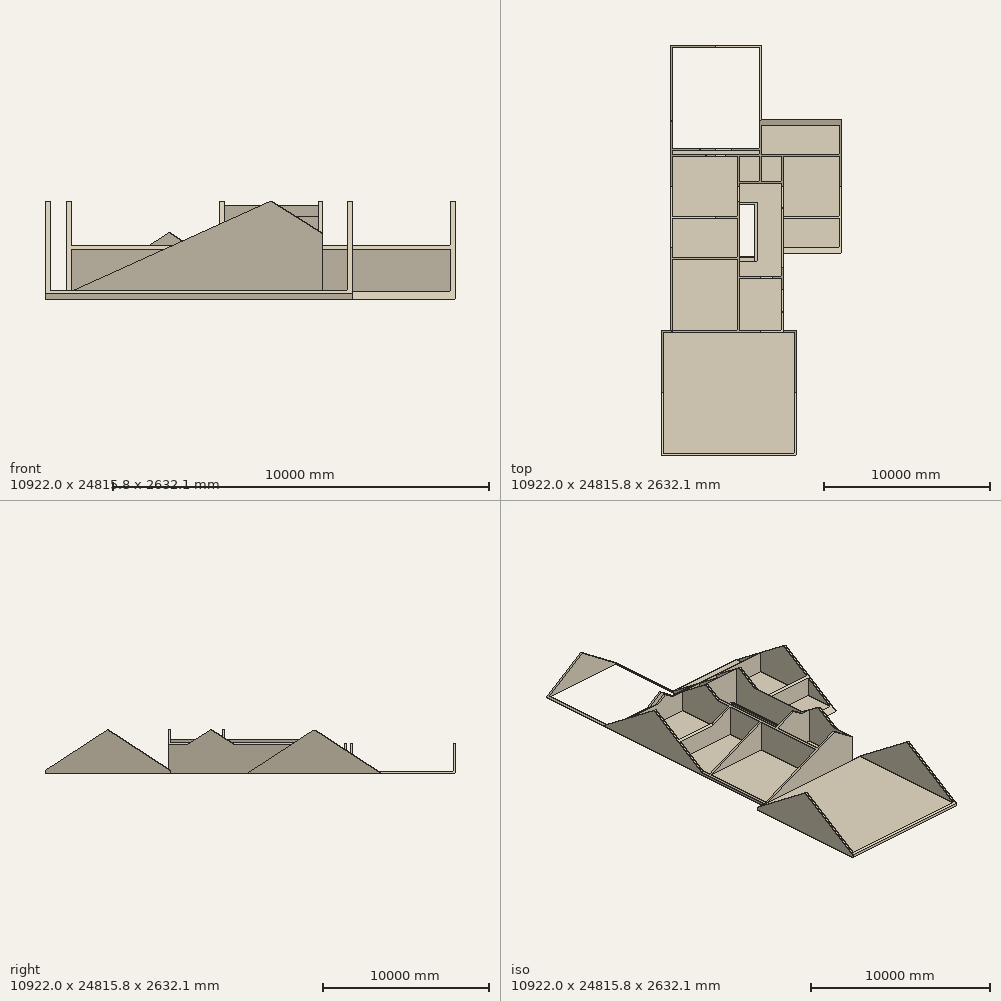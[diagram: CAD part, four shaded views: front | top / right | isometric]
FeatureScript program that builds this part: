
annotation { "Feature Type Name" : "Feature", "Feature Type Description" : "" }
export const myFeature = defineFeature(function(context is Context, id is Id, definition is map)
    precondition{}
    {
        {
            var Q0;
            Q0=qCreatedBy(makeId("Top.planeOp"),FACE);
            var sketch = newSketch(context, id + "F0", { "sketchPlane" : qUnion([Q0])});
            skLineSegment(sketch, "E0", {"start": v(0, 0) * mm, "end": v(8178.8, 0) * mm});
            skLineSegment(sketch, "E1", {"start": v(0, 0) * mm, "end": v(0, 7569.2) * mm});
            skLineSegment(sketch, "E2", {"start": v(0, 7569.2) * mm, "end": v(558.8, 7569.2) * mm});
            skLineSegment(sketch, "E3", {"start": v(558.8, 7569.2) * mm, "end": v(558.8, 24815.8) * mm});
            skLineSegment(sketch, "E4", {"start": v(558.8, 24815.8) * mm, "end": v(6045.2, 24815.8) * mm});
            skLineSegment(sketch, "E5", {"start": v(6045.2, 24815.8) * mm, "end": v(6045.2, 20548.6) * mm});
            skLineSegment(sketch, "E6", {"start": v(6045.2, 20548.6) * mm, "end": v(10922, 20548.6) * mm});
            skLineSegment(sketch, "E7", {"start": v(10922, 20548.6) * mm, "end": v(10922, 12014.2) * mm});
            skLineSegment(sketch, "E8", {"start": v(10922, 12014.2) * mm, "end": v(7391.4, 12014.2) * mm});
            skLineSegment(sketch, "E9", {"start": v(7391.4, 12014.2) * mm, "end": v(7391.4, 7569.2) * mm});
            skLineSegment(sketch, "E10", {"start": v(7391.4, 7569.2) * mm, "end": v(8178.8, 7569.2) * mm});
            skLineSegment(sketch, "E11", {"start": v(8178.8, 7569.2) * mm, "end": v(8178.8, 0) * mm});
            skSolve(sketch);
        }
        {
            var Q0;
            Q0=qSketchRegion(id+"F0",true);
            extrude(context, id + "F1", {"entities" : qUnion([Q0]), "depth" : 2632.07 * mm});
        }
        {
            var Q0;
            Q0=makeQuery(id+"F1.opExtrude","SWEPT_FACE",FACE,{"disambiguationData":[OSD([sQuery(id+"F0.wireOp",EDGE,"E7")])]});
            var sketch = newSketch(context, id + "F2", { "sketchPlane" : qUnion([Q0])});
            skLineSegment(sketch, "E12", {"start": v(16281.4, 2632.08) * mm, "end": v(16281.4, 219.08) * mm, "construction": true});
            skLineSegment(sketch, "E13", {"start": v(14452.6, 219.08) * mm, "end": v(18110.2, 219.08) * mm, "construction": true});
            skLineSegment(sketch, "E14", {"start": v(14452.6, 219.08) * mm, "end": v(14452.6, 1438.28) * mm, "construction": true});
            skLineSegment(sketch, "E15", {"start": v(16281.4, 2632.08) * mm, "end": v(12249.29, 0) * mm});
            skLineSegment(sketch, "E16", {"start": v(12249.29, 0) * mm, "end": v(12014.2, 0) * mm});
            skLineSegment(sketch, "E17", {"start": v(12014.2, 0) * mm, "end": v(12014.2, 2632.08) * mm});
            skLineSegment(sketch, "E18", {"start": v(12014.2, 2632.08) * mm, "end": v(16281.4, 2632.08) * mm});
            skLineSegment(sketch, "E19.MirrorCS", {"start": v(16281.4, 2632.08) * mm, "end": v(20313.51, 0) * mm});
            skLineSegment(sketch, "E20.MirrorCS", {"start": v(20313.51, 0) * mm, "end": v(20548.6, 0) * mm});
            skLineSegment(sketch, "E21.MirrorCS", {"start": v(20548.6, 0) * mm, "end": v(20548.6, 2632.08) * mm});
            skLineSegment(sketch, "E22.MirrorCS", {"start": v(20548.6, 2632.08) * mm, "end": v(16281.4, 2632.08) * mm});
            skLineSegment(sketch, "E23", {"start": v(3784.6, 2632.08) * mm, "end": v(3784.6, 219.08) * mm, "construction": true});
            skLineSegment(sketch, "E24", {"start": v(1955.8, 219.08) * mm, "end": v(5613.4, 219.08) * mm, "construction": true});
            skLineSegment(sketch, "E25", {"start": v(1955.8, 219.08) * mm, "end": v(1955.8, 1438.28) * mm, "construction": true});
            skLineSegment(sketch, "E26", {"start": v(3784.6, 2632.08) * mm, "end": v(0, 161.57) * mm});
            skLineSegment(sketch, "E27", {"start": v(0, 161.57) * mm, "end": v(0, 2632.08) * mm});
            skLineSegment(sketch, "E28", {"start": v(0, 2632.08) * mm, "end": v(3784.6, 2632.08) * mm});
            skLineSegment(sketch, "E29.MirrorCS", {"start": v(3784.6, 2632.08) * mm, "end": v(7569.2, 161.57) * mm});
            skLineSegment(sketch, "E30.MirrorCS", {"start": v(7569.2, 161.57) * mm, "end": v(7569.2, 2632.08) * mm});
            skLineSegment(sketch, "E31.MirrorCS", {"start": v(7569.2, 2632.08) * mm, "end": v(3784.6, 2632.08) * mm});
            skSolve(sketch);
        }
        {
            var Q0;
            Q0=qSketchRegion(id+"F2",true);
            var Q1;
            Q1=makeQuery(id+"F1.opExtrude","SWEPT_FACE",FACE,{"disambiguationData":[OSD([sQuery(id+"F0.wireOp",EDGE,"E1")])]});
            extrude(context, id + "F3", {"entities" : qUnion([Q0]), "operationType" : NewBodyOperationType.REMOVE, "endBound" : BoundingType.UP_TO_SURFACE, "oppositeDirection" : true, "endBoundEntityFace" : qUnion([Q1]), "depth" : 25.4 * mm});
        }
        {
            var Q0;
            Q0=makeQuery(id+"F3.boolean.opBoolean","COPY",FACE,{"derivedFrom":makeQuery(id+"F3.opExtrude","SWEPT_FACE",FACE,{"disambiguationData":[OSD([sQuery(id+"F2.wireOp",EDGE,"E30.MirrorCS")])]})});
            var sketch = newSketch(context, id + "F4", { "sketchPlane" : qUnion([Q0])});
            skLineSegment(sketch, "E32", {"start": v(6010.28, 2632.07) * mm, "end": v(6010.28, 219.07) * mm, "construction": true});
            skLineSegment(sketch, "E33", {"start": v(4756.15, 219.07) * mm, "end": v(7264.4, 219.07) * mm, "construction": true});
            skLineSegment(sketch, "E34", {"start": v(4756.15, 219.07) * mm, "end": v(4756.15, 1844.67) * mm, "construction": true});
            skLineSegment(sketch, "E35", {"start": v(6010.28, 2632.08) * mm, "end": v(558.8, 161.57) * mm});
            skLineSegment(sketch, "E36", {"start": v(558.8, 161.57) * mm, "end": v(558.8, 2632.07) * mm});
            skLineSegment(sketch, "E37", {"start": v(558.8, 2632.07) * mm, "end": v(6010.28, 2632.07) * mm});
            skLineSegment(sketch, "E38.MirrorCS", {"start": v(7264.4, 219.07) * mm, "end": v(7264.4, 1844.67) * mm, "construction": true});
            skLineSegment(sketch, "E39", {"start": v(6010.27, 2632.08) * mm, "end": v(7391.4, 1764.94) * mm});
            skLineSegment(sketch, "E40", {"start": v(7391.4, 1764.94) * mm, "end": v(7391.4, 2632.07) * mm});
            skLineSegment(sketch, "E41", {"start": v(7391.4, 2632.07) * mm, "end": v(6010.28, 2632.07) * mm});
            skSolve(sketch);
        }
        {
            var Q0;
            Q0=qSketchRegion(id+"F4",true);
            extrude(context, id + "F5", {"entities" : qUnion([Q0]), "operationType" : NewBodyOperationType.REMOVE, "endBound" : BoundingType.UP_TO_NEXT, "oppositeDirection" : true, "depth" : 25.4 * mm});
        }
        {
            var Q0;
            Q0=makeQuery(id+"F3.boolean.opBoolean","COPY",FACE,{"derivedFrom":makeQuery(id+"F3.opExtrude","SWEPT_FACE",FACE,{"disambiguationData":[OSD([sQuery(id+"F2.wireOp",EDGE,"E30.MirrorCS")])]})});
            var sketch = newSketch(context, id + "F6", { "sketchPlane" : qUnion([Q0])});
            skLineSegment(sketch, "E42", {"start": v(558.8, 161.57) * mm, "end": v(6010.28, 2632.08) * mm});
            skLineSegment(sketch, "E43", {"start": v(6010.28, 2632.08) * mm, "end": v(7391.4, 1764.94) * mm});
            skLineSegment(sketch, "E44", {"start": v(7391.4, 1764.94) * mm, "end": v(7391.4, 161.57) * mm});
            skLineSegment(sketch, "E45", {"start": v(7391.4, 161.57) * mm, "end": v(558.8, 161.57) * mm});
            skSolve(sketch);
        }
        {
            var Q0;
            Q0=qSketchRegion(id+"F6",true);
            extrude(context, id + "F7", {"entities" : qUnion([Q0]), "operationType" : NewBodyOperationType.ADD, "endBound" : BoundingType.UP_TO_NEXT, "depth" : 25.4 * mm});
        }
        {
            var Q0;
            Q0=makeQuery(id+"F3.boolean.opBoolean","COPY",FACE,{"derivedFrom":makeQuery(id+"F3.opExtrude","SWEPT_FACE",FACE,{"disambiguationData":[OSD([sQuery(id+"F2.wireOp",EDGE,"E17")])]})});
            var sketch = newSketch(context, id + "F8", { "sketchPlane" : qUnion([Q0])});
            skLineSegment(sketch, "E46", {"start": v(-6010.27, 2632.08) * mm, "end": v(-7391.4, 1764.94) * mm});
            skLineSegment(sketch, "E47", {"start": v(-7391.4, 1764.94) * mm, "end": v(-7391.4, 0) * mm});
            skLineSegment(sketch, "E48", {"start": v(-7391.4, 0) * mm, "end": v(-558.8, 0) * mm});
            skLineSegment(sketch, "E49", {"start": v(-558.8, 161.57) * mm, "end": v(-6010.27, 2632.08) * mm});
            skLineSegment(sketch, "E50", {"start": v(-558.8, 161.57) * mm, "end": v(-558.8, 0) * mm});
            skSolve(sketch);
        }
        {
            var Q0;
            Q0=qSketchRegion(id+"F8",true);
            extrude(context, id + "F9", {"entities" : qUnion([Q0]), "operationType" : NewBodyOperationType.ADD, "endBound" : BoundingType.UP_TO_NEXT, "depth" : 25.4 * mm});
        }
        {
            var Q0;
            Q0=makeQuery(id+"F1.opExtrude","SWEPT_FACE",FACE,{"disambiguationData":[OSD([sQuery(id+"F0.wireOp",EDGE,"E4")])]});
            var sketch = newSketch(context, id + "F10", { "sketchPlane" : qUnion([Q0])});
            skLineSegment(sketch, "E51", {"start": v(-3302, 2632.08) * mm, "end": v(-3302, 0) * mm, "construction": true});
            skPoint(sketch, "E52", {"position": v(-3302, 219.07) * mm});
            skPoint(sketch, "E53", {"position": v(-3302, 1793.88) * mm});
            skLineSegment(sketch, "E54", {"start": v(-5130.8, 219.07) * mm, "end": v(-1473.2, 219.07) * mm, "construction": true});
            skLineSegment(sketch, "E55", {"start": v(-5130.8, 219.08) * mm, "end": v(-5130.8, 1438.27) * mm, "construction": true});
            skLineSegment(sketch, "E56", {"start": v(-5130.8, 1438.27) * mm, "end": v(-3302, 2632.08) * mm, "construction": true});
            skLineSegment(sketch, "E57", {"start": v(-3302, 1793.88) * mm, "end": v(-6045.2, 3.17) * mm});
            skLineSegment(sketch, "E58", {"start": v(-6045.2, 3.17) * mm, "end": v(-6045.2, 2632.08) * mm});
            skLineSegment(sketch, "E59", {"start": v(-6045.2, 2632.08) * mm, "end": v(-3302, 2632.08) * mm});
            skLineSegment(sketch, "E60.MirrorCS", {"start": v(-3302, 1793.88) * mm, "end": v(-558.8, 3.17) * mm});
            skLineSegment(sketch, "E61.MirrorCS", {"start": v(-558.8, 3.17) * mm, "end": v(-558.8, 2632.08) * mm});
            skLineSegment(sketch, "E62.MirrorCS", {"start": v(-558.8, 2632.08) * mm, "end": v(-3302, 2632.08) * mm});
            skSolve(sketch);
        }
        {
            var Q0;
            Q0=qSketchRegion(id+"F10",true);
            extrude(context, id + "F11", {"entities" : qUnion([Q0]), "operationType" : NewBodyOperationType.REMOVE, "endBound" : BoundingType.UP_TO_NEXT, "oppositeDirection" : true, "depth" : 25.4 * mm});
        }
        {
            var Q0;
            Q0=makeQuery(id+"F3.boolean.opBoolean","COPY",FACE,{"derivedFrom":makeQuery(id+"F3.opExtrude","SWEPT_FACE",FACE,{"disambiguationData":[OSD([sQuery(id+"F2.wireOp",EDGE,"E21.MirrorCS")])]})});
            var sketch = newSketch(context, id + "F12", { "sketchPlane" : qUnion([Q0])});
            skLineSegment(sketch, "E63", {"start": v(3302, 1793.88) * mm, "end": v(558.8, 3.17) * mm});
            skLineSegment(sketch, "E64", {"start": v(558.8, 3.17) * mm, "end": v(558.8, 0) * mm});
            skLineSegment(sketch, "E65", {"start": v(558.8, 0) * mm, "end": v(6045.2, 0) * mm});
            skLineSegment(sketch, "E66", {"start": v(6045.2, 0) * mm, "end": v(6045.2, 3.17) * mm});
            skLineSegment(sketch, "E67", {"start": v(6045.2, 3.17) * mm, "end": v(3302, 1793.88) * mm});
            skSolve(sketch);
        }
        {
            var Q0;
            Q0=qSketchRegion(id+"F12",true);
            extrude(context, id + "F13", {"entities" : qUnion([Q0]), "operationType" : NewBodyOperationType.ADD, "endBound" : BoundingType.UP_TO_NEXT, "depth" : 25.4 * mm});
        }
        {
            var Q0;
            Q0=makeQuery(id+"F9.boolean.opBoolean","MERGE",FACE,{"derivedFrom":[makeQuery(id+"F7.boolean.opBoolean","MERGE",FACE,{"derivedFrom":[makeQuery(id+"F1.opExtrude","SWEPT_FACE",FACE,{"disambiguationData":[OSD([sQuery(id+"F0.wireOp",EDGE,"E9")])]}),makeQuery(id+"F7.opExtrude","SWEPT_FACE",FACE,{"disambiguationData":[OSD([sQuery(id+"F6.wireOp",EDGE,"E44")])]})]}),makeQuery(id+"F9.opExtrude","SWEPT_FACE",FACE,{"disambiguationData":[OSD([sQuery(id+"F8.wireOp",EDGE,"E47")])]})]});
            var sketch = newSketch(context, id + "F14", { "sketchPlane" : qUnion([Q0])});
            skLineSegment(sketch, "E68", {"start": v(3784.6, 2632.08) * mm, "end": v(16281.4, 2632.08) * mm, "construction": true});
            skLineSegment(sketch, "E69", {"start": v(10033, 2632.08) * mm, "end": v(10033, 0) * mm, "construction": true});
            skLineSegment(sketch, "E70", {"start": v(8778.88, 219.08) * mm, "end": v(11287.13, 219.08) * mm, "construction": true});
            skPoint(sketch, "E71", {"position": v(10033, 219.08) * mm});
            skLineSegment(sketch, "E72", {"start": v(8778.88, 219.08) * mm, "end": v(8778.88, 1844.68) * mm, "construction": true});
            skLineSegment(sketch, "E73", {"start": v(10033, 2632.07) * mm, "end": v(8651.87, 1764.94) * mm});
            skLineSegment(sketch, "E74.MirrorCS", {"start": v(10033, 2632.07) * mm, "end": v(11414.13, 1764.94) * mm});
            skLineSegment(sketch, "E75", {"start": v(8651.87, 1764.94) * mm, "end": v(11414.13, 1764.94) * mm});
            skSolve(sketch);
        }
        {
            var Q0;
            Q0=qSketchRegion(id+"F14",true);
            extrude(context, id + "F15", {"entities" : qUnion([Q0]), "operationType" : NewBodyOperationType.ADD, "endBound" : BoundingType.UP_TO_NEXT, "oppositeDirection" : true, "depth" : 25.4 * mm});
        }
        {
            var Q0;
            Q0=qCreatedBy(makeId("Top.planeOp"),FACE);
            cPlane(context, id + "F16", {"entities" : qUnion([Q0]), "cplaneType" : CPlaneType.OFFSET, "offset" : 2632.07 * mm, "width" : 152.4 * mm, "height" : 152.4 * mm});
        }
        {
            var Q0;
            Q0=qCreatedBy(id+"F16.planeOp",FACE);
            var sketch = newSketch(context, id + "F17", { "sketchPlane" : qUnion([Q0])});
            skLineSegment(sketch, "E76.bottom", {"start": v(685.8, 24688.8) * mm, "end": v(5918.2, 24688.8) * mm});
            skLineSegment(sketch, "E76.top", {"start": v(685.8, 18592.8) * mm, "end": v(5918.2, 18592.8) * mm});
            skLineSegment(sketch, "E76.left", {"start": v(685.8, 24688.8) * mm, "end": v(685.8, 18592.8) * mm});
            skLineSegment(sketch, "E76.right", {"start": v(5918.2, 24688.8) * mm, "end": v(5918.2, 18592.8) * mm});
            skSolve(sketch);
        }
        {
            var Q0;
            Q0=qSketchRegion(id+"F17",true);
            extrude(context, id + "F18", {"entities" : qUnion([Q0]), "operationType" : NewBodyOperationType.REMOVE, "endBound" : BoundingType.THROUGH_ALL, "oppositeDirection" : true, "depth" : 25.4 * mm});
        }
        {
            var Q0;
            Q0=qCreatedBy(id+"F16.planeOp",FACE);
            var sketch = newSketch(context, id + "F19", { "sketchPlane" : qUnion([Q0])});
            skLineSegment(sketch, "E77.bottom", {"start": v(7391.4, 18110.2) * mm, "end": v(10795, 18110.2) * mm});
            skLineSegment(sketch, "E77.top", {"start": v(7391.4, 14452.6) * mm, "end": v(10795, 14452.6) * mm});
            skLineSegment(sketch, "E77.left", {"start": v(7391.4, 18110.2) * mm, "end": v(7391.4, 14452.6) * mm});
            skLineSegment(sketch, "E77.right", {"start": v(10795, 18110.2) * mm, "end": v(10795, 14452.6) * mm});
            skLineSegment(sketch, "E78", {"start": v(10922, 16281.4) * mm, "end": v(558.8, 16281.4) * mm, "construction": true});
            skPoint(sketch, "E79", {"position": v(10795, 16281.4) * mm});
            skLineSegment(sketch, "E80.bottom", {"start": v(685.8, 18110.2) * mm, "end": v(4629.15, 18110.2) * mm});
            skLineSegment(sketch, "E80.top", {"start": v(685.8, 14452.6) * mm, "end": v(4629.15, 14452.6) * mm});
            skLineSegment(sketch, "E80.left", {"start": v(685.8, 18110.2) * mm, "end": v(685.8, 14452.6) * mm});
            skLineSegment(sketch, "E80.right", {"start": v(4629.15, 18110.2) * mm, "end": v(4629.15, 14452.6) * mm});
            skLineSegment(sketch, "E81.bottom", {"start": v(4756.15, 18110.2) * mm, "end": v(5946.77, 18110.2) * mm});
            skLineSegment(sketch, "E81.top", {"start": v(4756.15, 16586.2) * mm, "end": v(5946.77, 16586.2) * mm});
            skLineSegment(sketch, "E81.left", {"start": v(4756.15, 18110.2) * mm, "end": v(4756.15, 16586.2) * mm});
            skLineSegment(sketch, "E81.right", {"start": v(5946.77, 18110.2) * mm, "end": v(5946.77, 16586.2) * mm});
            skLineSegment(sketch, "E82.bottom", {"start": v(7264.4, 18110.2) * mm, "end": v(6073.77, 18110.2) * mm});
            skLineSegment(sketch, "E82.top", {"start": v(7264.4, 16586.2) * mm, "end": v(6073.77, 16586.2) * mm});
            skLineSegment(sketch, "E82.left", {"start": v(7264.4, 18110.2) * mm, "end": v(7264.4, 16586.2) * mm});
            skLineSegment(sketch, "E82.right", {"start": v(6073.77, 18110.2) * mm, "end": v(6073.77, 16586.2) * mm});
            skLineSegment(sketch, "E83.bottom", {"start": v(10795, 14325.6) * mm, "end": v(7391.4, 14325.6) * mm});
            skLineSegment(sketch, "E83.top", {"start": v(10795, 12014.2) * mm, "end": v(7391.4, 12014.2) * mm});
            skLineSegment(sketch, "E83.left", {"start": v(10795, 14325.6) * mm, "end": v(10795, 12014.2) * mm});
            skLineSegment(sketch, "E83.right", {"start": v(7391.4, 14325.6) * mm, "end": v(7391.4, 12014.2) * mm});
            skLineSegment(sketch, "E84.bottom", {"start": v(10795, 18237.2) * mm, "end": v(6045.2, 18237.2) * mm});
            skLineSegment(sketch, "E84.top", {"start": v(10795, 20548.6) * mm, "end": v(6045.2, 20548.6) * mm});
            skLineSegment(sketch, "E84.left", {"start": v(10795, 18237.2) * mm, "end": v(10795, 20548.6) * mm});
            skLineSegment(sketch, "E84.right", {"start": v(6045.2, 18237.2) * mm, "end": v(6045.2, 20548.6) * mm});
            skLineSegment(sketch, "E85.bottom", {"start": v(685.8, 18237.2) * mm, "end": v(5918.2, 18237.2) * mm});
            skLineSegment(sketch, "E85.top", {"start": v(685.8, 18465.8) * mm, "end": v(5918.2, 18465.8) * mm});
            skLineSegment(sketch, "E85.left", {"start": v(685.8, 18237.2) * mm, "end": v(685.8, 18465.8) * mm});
            skLineSegment(sketch, "E85.right", {"start": v(5918.2, 18237.2) * mm, "end": v(5918.2, 18465.8) * mm});
            skLineSegment(sketch, "E86.bottom", {"start": v(685.8, 14325.6) * mm, "end": v(4629.15, 14325.6) * mm});
            skLineSegment(sketch, "E86.top", {"start": v(685.8, 12014.2) * mm, "end": v(4629.15, 12014.2) * mm});
            skLineSegment(sketch, "E86.left", {"start": v(685.8, 14325.6) * mm, "end": v(685.8, 12014.2) * mm});
            skLineSegment(sketch, "E86.right", {"start": v(4629.15, 14325.6) * mm, "end": v(4629.15, 12014.2) * mm});
            skLineSegment(sketch, "E87.bottom", {"start": v(127, 7442.2) * mm, "end": v(8051.8, 7442.2) * mm});
            skLineSegment(sketch, "E87.top", {"start": v(127, 127) * mm, "end": v(8051.8, 127) * mm});
            skLineSegment(sketch, "E87.left", {"start": v(127, 7442.2) * mm, "end": v(127, 127) * mm});
            skLineSegment(sketch, "E87.right", {"start": v(8051.8, 7442.2) * mm, "end": v(8051.8, 127) * mm});
            skLineSegment(sketch, "E88.bottom", {"start": v(685.8, 11887.2) * mm, "end": v(4629.15, 11887.2) * mm});
            skLineSegment(sketch, "E88.top", {"start": v(685.8, 7569.2) * mm, "end": v(4629.15, 7569.2) * mm});
            skLineSegment(sketch, "E88.left", {"start": v(685.8, 11887.2) * mm, "end": v(685.8, 7569.2) * mm});
            skLineSegment(sketch, "E88.right", {"start": v(4629.15, 11887.2) * mm, "end": v(4629.15, 7569.2) * mm});
            skLineSegment(sketch, "E89.bottom", {"start": v(4756.15, 16459.2) * mm, "end": v(7264.4, 16459.2) * mm});
            skLineSegment(sketch, "E89.top", {"start": v(4756.15, 10820.4) * mm, "end": v(7264.4, 10820.4) * mm});
            skLineSegment(sketch, "E89.left", {"start": v(4756.15, 16459.2) * mm, "end": v(4756.15, 10820.4) * mm});
            skLineSegment(sketch, "E89.right", {"start": v(7264.4, 16459.2) * mm, "end": v(7264.4, 10820.4) * mm});
            skLineSegment(sketch, "E90.bottom", {"start": v(4756.15, 10693.4) * mm, "end": v(7264.4, 10693.4) * mm});
            skLineSegment(sketch, "E90.top", {"start": v(4756.15, 7569.2) * mm, "end": v(7264.4, 7569.2) * mm});
            skLineSegment(sketch, "E90.left", {"start": v(4756.15, 10693.4) * mm, "end": v(4756.15, 7569.2) * mm});
            skLineSegment(sketch, "E90.right", {"start": v(7264.4, 10693.4) * mm, "end": v(7264.4, 7569.2) * mm});
            skSolve(sketch);
        }
        {
            var Q0;
            Q0=qSketchRegion(id+"F19",true);
            extrude(context, id + "F20", {"entities" : qUnion([Q0]), "operationType" : NewBodyOperationType.REMOVE, "oppositeDirection" : true, "depth" : 2413 * mm});
        }
        {
            var Q0;
            Q0=makeQuery(id+"F20.boolean.opBoolean","COPY",FACE,{"derivedFrom":makeQuery(id+"F20.opExtrude","CAP_FACE",FACE,{"disambiguationData":[OSD([sQuery(id+"F19.wireOp",EDGE,"E89.bottom"),sQuery(id+"F19.wireOp",EDGE,"E89.top"),sQuery(id+"F19.wireOp",EDGE,"E89.left"),sQuery(id+"F19.wireOp",EDGE,"E89.right")])],"isStart":false})});
            var sketch = newSketch(context, id + "F21", { "sketchPlane" : qUnion([Q0])});
            skLineSegment(sketch, "E91.bottom", {"start": v(4756.15, 15214.6) * mm, "end": v(5670.55, 15214.6) * mm});
            skLineSegment(sketch, "E91.top", {"start": v(4756.15, 11734.8) * mm, "end": v(5670.55, 11734.8) * mm});
            skLineSegment(sketch, "E91.left", {"start": v(4756.15, 15214.6) * mm, "end": v(4756.15, 11734.8) * mm});
            skLineSegment(sketch, "E91.right", {"start": v(5670.55, 15214.6) * mm, "end": v(5670.55, 11734.8) * mm});
            skSolve(sketch);
        }
        {
            var Q0;
            Q0=qSketchRegion(id+"F21",true);
            extrude(context, id + "F22", {"entities" : qUnion([Q0]), "operationType" : NewBodyOperationType.REMOVE, "endBound" : BoundingType.THROUGH_ALL, "oppositeDirection" : true, "depth" : 25.4 * mm});
        }
        {
            var Q0;
            Q0=makeQuery(id+"F22.boolean.opBoolean","MERGE",FACE,{"derivedFrom":[makeQuery(id+"F20.boolean.opBoolean","COPY",FACE,{"derivedFrom":makeQuery(id+"F20.opExtrude","SWEPT_FACE",FACE,{"disambiguationData":[OSD([sQuery(id+"F19.wireOp",EDGE,"E89.left")])]})}),makeQuery(id+"F22.opExtrude","SWEPT_FACE",FACE,{"disambiguationData":[OSD([sQuery(id+"F21.wireOp",EDGE,"E91.left")])]})]});
            var sketch = newSketch(context, id + "F23", { "sketchPlane" : qUnion([Q0])});
            skLineSegment(sketch, "E92.bottom", {"start": v(11734.8, 28.57) * mm, "end": v(12014.2, 28.57) * mm});
            skLineSegment(sketch, "E92.top", {"start": v(11734.8, 0) * mm, "end": v(12014.2, 0) * mm});
            skLineSegment(sketch, "E92.left", {"start": v(11734.8, 28.58) * mm, "end": v(11734.8, 0) * mm});
            skLineSegment(sketch, "E92.right", {"start": v(12014.2, 28.57) * mm, "end": v(12014.2, 0) * mm});
            skSolve(sketch);
        }
        {
            var Q0;
            Q0=qSketchRegion(id+"F23",true);
            extrude(context, id + "F24", {"entities" : qUnion([Q0]), "operationType" : NewBodyOperationType.ADD, "endBound" : BoundingType.UP_TO_NEXT, "depth" : 25.4 * mm});
        }
        {
            var Q0;
            Q0=makeQuery(id+"F20.boolean.opBoolean","COPY",FACE,{"derivedFrom":makeQuery(id+"F20.opExtrude","CAP_FACE",FACE,{"disambiguationData":[OSD([sQuery(id+"F19.wireOp",EDGE,"E89.bottom"),sQuery(id+"F19.wireOp",EDGE,"E89.top"),sQuery(id+"F19.wireOp",EDGE,"E89.left"),sQuery(id+"F19.wireOp",EDGE,"E89.right")])],"isStart":false})});
            var sketch = newSketch(context, id + "F25", { "sketchPlane" : qUnion([Q0])});
            skLineSegment(sketch, "E93", {"start": v(4756.15, 15214.6) * mm, "end": v(4756.15, 15341.6) * mm});
            skLineSegment(sketch, "E94", {"start": v(4756.15, 15341.6) * mm, "end": v(5797.55, 15341.6) * mm});
            skLineSegment(sketch, "E95", {"start": v(5797.55, 15341.6) * mm, "end": v(5797.55, 11734.8) * mm});
            skLineSegment(sketch, "E96", {"start": v(5797.55, 11734.8) * mm, "end": v(5670.55, 11734.8) * mm});
            skLineSegment(sketch, "E97", {"start": v(5670.55, 11734.8) * mm, "end": v(5670.55, 15214.6) * mm});
            skLineSegment(sketch, "E98", {"start": v(5670.55, 15214.6) * mm, "end": v(4756.15, 15214.6) * mm});
            skSolve(sketch);
        }
        {
            var Q0;
            Q0=qSketchRegion(id+"F25",true);
            extrude(context, id + "F26", {"entities" : qUnion([Q0]), "operationType" : NewBodyOperationType.ADD, "depth" : 1219.2 * mm});
        }
        {
            var Q0;
            Q0=qCreatedBy(makeId("Top.planeOp"),FACE);
            cPlane(context, id + "F28", {"entities" : qUnion([Q0]), "cplaneType" : CPlaneType.OFFSET, "offset" : 2946.4 * mm, "width" : 152.4 * mm, "height" : 152.4 * mm});
        }
    });
